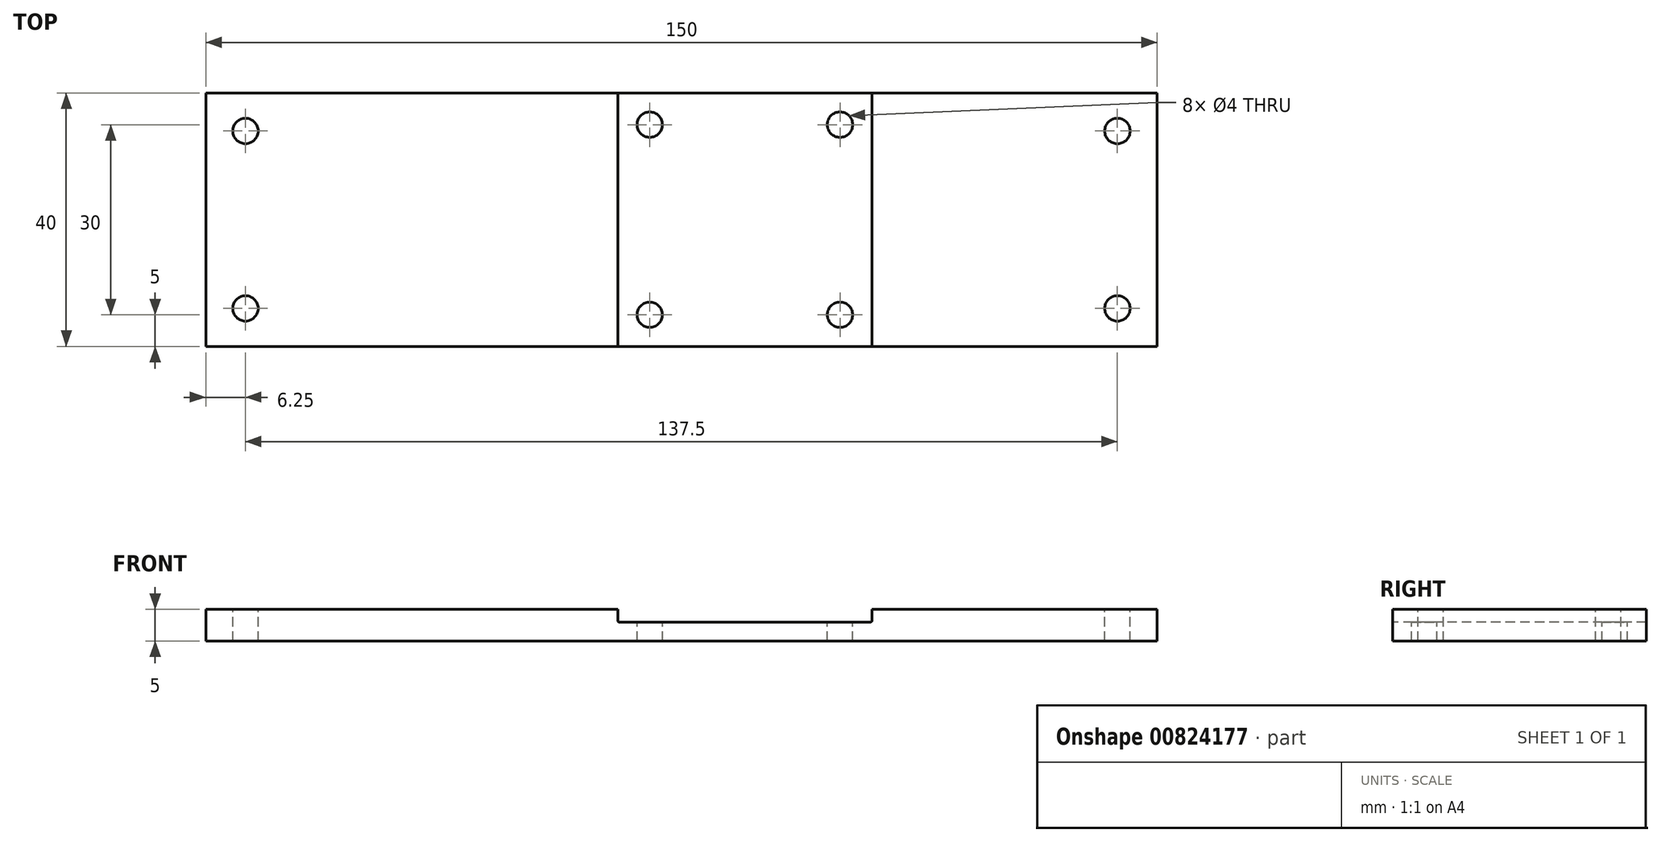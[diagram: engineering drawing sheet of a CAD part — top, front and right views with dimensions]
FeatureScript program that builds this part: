
annotation { "Feature Type Name" : "Feature", "Feature Type Description" : "" }
export const myFeature = defineFeature(function(context is Context, id is Id, definition is map)
    precondition{}
    {
        {
            var Q0;
            Q0=qCreatedBy(makeId("Top.planeOp"),FACE);
            var sketch = newSketch(context, id + "F0", { "sketchPlane" : qUnion([Q0])});
            skLineSegment(sketch, "E0.bottom", {"start": v(0, 0) * mm, "end": v(150, 0) * mm});
            skLineSegment(sketch, "E0.top", {"start": v(0, 40) * mm, "end": v(150, 40) * mm});
            skLineSegment(sketch, "E0.left", {"start": v(0, 0) * mm, "end": v(0, 40) * mm});
            skLineSegment(sketch, "E0.right", {"start": v(150, 0) * mm, "end": v(150, 40) * mm});
            skSolve(sketch);
        }
        {
            var Q0;
            Q0 = qSketchRegion(id + "F0", true);
            extrude(context, id + "F1", {"entities" : qUnion([Q0]), "depth" : 5 * mm, "offsetDistance" : 25 * mm});
        }
        {
            var Q0;
            Q0=makeQuery(id+"F1.opExtrude","CAP_FACE",FACE,{"disambiguationData":[OSD([sQuery(id+"F0.wireOp",EDGE,"E0.bottom"),sQuery(id+"F0.wireOp",EDGE,"E0.top"),sQuery(id+"F0.wireOp",EDGE,"E0.left"),sQuery(id+"F0.wireOp",EDGE,"E0.right")])],"isStart":false});
            var sketch = newSketch(context, id + "F2", { "sketchPlane" : qUnion([Q0])});
            skLineSegment(sketch, "E1", {"start": v(6.25, 40) * mm, "end": v(6.25, 0) * mm, "construction": true});
            skLineSegment(sketch, "E2", {"start": v(143.75, 40) * mm, "end": v(143.75, 0) * mm, "construction": true});
            skCircle(sketch, "E3", {"center": v(6.25, 34) * mm, "radius": 2 * mm});
            skCircle(sketch, "E4.0.1.0", {"center": v(6.25, 6) * mm, "radius": 2 * mm});
            skCircle(sketch, "E4.1.0.0", {"center": v(143.75, 34) * mm, "radius": 2 * mm});
            skCircle(sketch, "E4.1.1.0", {"center": v(143.75, 6) * mm, "radius": 2 * mm});
            skLineSegment(sketch, "E4.direction1", {"start": v(6.25, 34) * mm, "end": v(143.75, 34) * mm, "construction": true});
            skLineSegment(sketch, "E4.direction2", {"start": v(6.25, 34) * mm, "end": v(6.25, 6) * mm, "construction": true});
            skSolve(sketch);
        }
        {
            var Q0;
            Q0 = qSketchRegion(id + "F2", true);
            extrude(context, id + "F3", {"entities" : qUnion([Q0]), "operationType" : NewBodyOperationType.REMOVE, "oppositeDirection" : true, "depth" : 25 * mm, "offsetDistance" : 25 * mm});
        }
        {
            var Q0;
            Q0=makeQuery(id+"F1.opExtrude","CAP_FACE",FACE,{"disambiguationData":[OSD([sQuery(id+"F0.wireOp",EDGE,"E0.bottom"),sQuery(id+"F0.wireOp",EDGE,"E0.top"),sQuery(id+"F0.wireOp",EDGE,"E0.left"),sQuery(id+"F0.wireOp",EDGE,"E0.right")])],"isStart":false});
            var sketch = newSketch(context, id + "F4", { "sketchPlane" : qUnion([Q0])});
            skLineSegment(sketch, "E5", {"start": v(70, 40) * mm, "end": v(70, 0) * mm, "construction": true});
            skCircle(sketch, "E6", {"center": v(70, 35) * mm, "radius": 2 * mm});
            skCircle(sketch, "E7.0.1.0", {"center": v(70, 5) * mm, "radius": 2 * mm});
            skCircle(sketch, "E7.1.0.0", {"center": v(100, 35) * mm, "radius": 2 * mm});
            skCircle(sketch, "E7.1.1.0", {"center": v(100, 5) * mm, "radius": 2 * mm});
            skLineSegment(sketch, "E7.direction1", {"start": v(70, 35) * mm, "end": v(100, 35) * mm, "construction": true});
            skLineSegment(sketch, "E7.direction2", {"start": v(70, 35) * mm, "end": v(70, 5) * mm, "construction": true});
            skSolve(sketch);
        }
        {
            var Q0;
            Q0 = qSketchRegion(id + "F4", true);
            extrude(context, id + "F5", {"entities" : qUnion([Q0]), "operationType" : NewBodyOperationType.REMOVE, "oppositeDirection" : true, "depth" : 25 * mm, "offsetDistance" : 25 * mm});
        }
        {
            var Q0;
            Q0=makeQuery(id+"F1.opExtrude","CAP_FACE",FACE,{"disambiguationData":[OSD([sQuery(id+"F0.wireOp",EDGE,"E0.bottom"),sQuery(id+"F0.wireOp",EDGE,"E0.top"),sQuery(id+"F0.wireOp",EDGE,"E0.left"),sQuery(id+"F0.wireOp",EDGE,"E0.right")])],"isStart":false});
            var sketch = newSketch(context, id + "F6", { "sketchPlane" : qUnion([Q0])});
            skLineSegment(sketch, "E8.bottom", {"start": v(64.95, 40) * mm, "end": v(105.05, 40) * mm});
            skLineSegment(sketch, "E8.top", {"start": v(64.95, 0) * mm, "end": v(105.05, 0) * mm});
            skLineSegment(sketch, "E8.left", {"start": v(64.95, 40) * mm, "end": v(64.95, 0) * mm});
            skLineSegment(sketch, "E8.right", {"start": v(105.05, 40) * mm, "end": v(105.05, 0) * mm});
            skLineSegment(sketch, "E9", {"start": v(85, 40) * mm, "end": v(85, 0) * mm, "construction": true});
            skLineSegment(sketch, "E10", {"start": v(70, 35) * mm, "end": v(70, 5) * mm, "construction": true});
            skSolve(sketch);
        }
        {
            var Q0;
            Q0 = qSketchRegion(id + "F6", true);
            extrude(context, id + "F7", {"entities" : qUnion([Q0]), "operationType" : NewBodyOperationType.REMOVE, "oppositeDirection" : true, "depth" : 2 * mm, "offsetDistance" : 25 * mm});
        }
        {
            var Q0;
            Q0=makeQuery(id+"F7.boolean.opBoolean","COPY",EDGE,{"derivedFrom":makeQuery(id+"F7.opExtrude","CAP_EDGE",EDGE,{"disambiguationData":[OSD([sQuery(id+"F6.wireOp",EDGE,"E8.left")])],"isStart":true})});
            var Q1;
            Q1=makeQuery(id+"F7.boolean.opBoolean","COPY",EDGE,{"derivedFrom":makeQuery(id+"F7.opExtrude","CAP_EDGE",EDGE,{"disambiguationData":[OSD([sQuery(id+"F6.wireOp",EDGE,"E8.left")])],"isStart":false})});
            var Q2;
            Q2=makeQuery(id+"F7.boolean.opBoolean","COPY",EDGE,{"derivedFrom":makeQuery(id+"F7.opExtrude","CAP_EDGE",EDGE,{"disambiguationData":[OSD([sQuery(id+"F6.wireOp",EDGE,"E8.right")])],"isStart":true})});
            var Q3;
            Q3=makeQuery(id+"F7.boolean.opBoolean","COPY",EDGE,{"derivedFrom":makeQuery(id+"F7.opExtrude","CAP_EDGE",EDGE,{"disambiguationData":[OSD([sQuery(id+"F6.wireOp",EDGE,"E8.right")])],"isStart":false})});
            fillet(context, id + "F8", {"entities" : qUnion([Q0, Q1, Q2, Q3]), "radius" : 0.25 * mm, "tangentPropagation" : true, "allowEdgeOverflow" : false});
        }
    });
